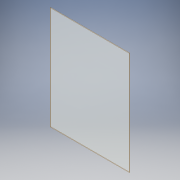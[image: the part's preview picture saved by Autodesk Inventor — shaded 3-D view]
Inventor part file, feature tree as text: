
AUTODESK INVENTOR PART (.ipt)
format: ipt  version: 2018 (Build 220112000, 112)  size: 96,768 bytes
history: native  units: in
note: dims shown in document units (in); Inventor stores cm internally (conversion verified against a paired STEP export)
features: extrude x1, sketch x1
ambient origin geometry x8: Origin, YZ Plane, XZ Plane, XY Plane, X Axis, Y Axis, Z Axis, Center Point
bodies: Solid1 (feature_tree)
feature tree (2):
  extrude  "Extrusion1"  Depth=22.25in
  sketch  "Sketch1"  dims[d0=17.0in d1=22.25in d2=0.125in d3=0.0in]
